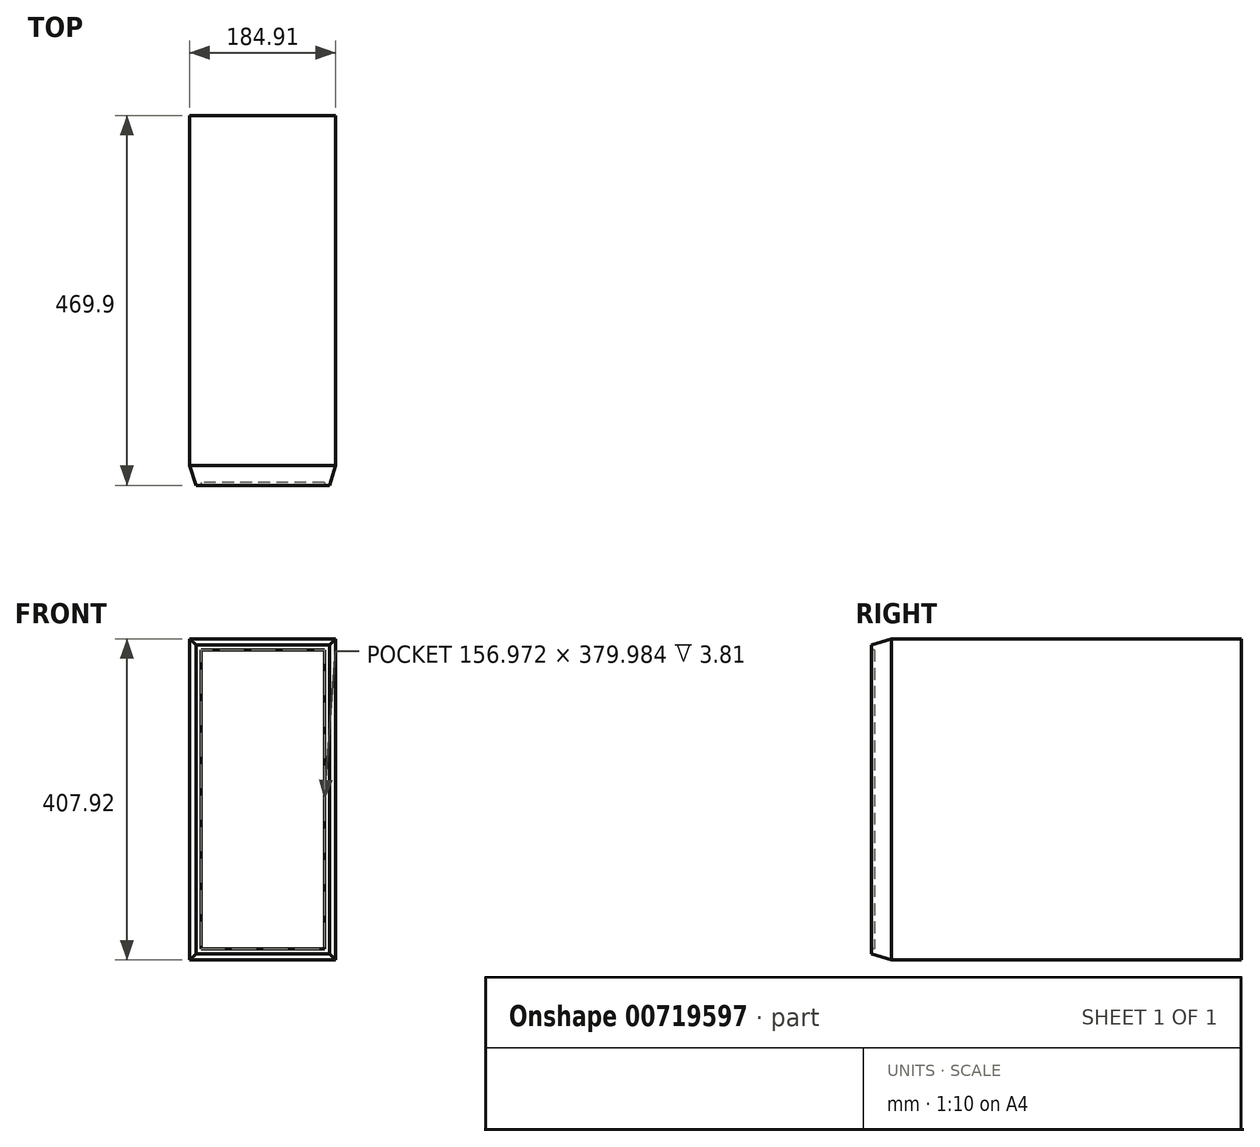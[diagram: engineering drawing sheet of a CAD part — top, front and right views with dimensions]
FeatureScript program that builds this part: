
annotation { "Feature Type Name" : "Feature", "Feature Type Description" : "" }
export const myFeature = defineFeature(function(context is Context, id is Id, definition is map)
    precondition{}
    {
        {
            var Q0;
            Q0=qCreatedBy(makeId("Front.planeOp"),FACE);
            var sketch = newSketch(context, id + "F0", { "sketchPlane" : qUnion([Q0])});
            skPoint(sketch, "E0.0", {"position": v(0, 0) * mm});
            skLineSegment(sketch, "E1.bottom", {"start": v(0, 0) * mm, "end": v(184.91, 0) * mm});
            skLineSegment(sketch, "E1.top", {"start": v(0, 407.92) * mm, "end": v(184.91, 407.92) * mm});
            skLineSegment(sketch, "E1.left", {"start": v(0, 0) * mm, "end": v(0, 407.92) * mm});
            skLineSegment(sketch, "E1.right", {"start": v(184.91, 0) * mm, "end": v(184.91, 407.92) * mm});
            skSolve(sketch);
        }
        {
            var Q0;
            Q0=makeQuery(id+"F0.imprint","IMPRINT",FACE,{"disambiguationData":[TD([[makeQuery(id+"F0.imprint","IMPRINT",EDGE,{"derivedFrom":sQuery(id+"F0.wireOp",EDGE,"E1.bottom")}),1.0]])]});
            extrude(context, id + "F1", {"entities" : qUnion([Q0]), "oppositeDirection" : true, "depth" : 469.9 * mm, "offsetDistance" : 25.4 * mm});
        }
        {
            var Q0;
            Q0=makeQuery(id+"F1.opExtrude","CAP_EDGE",EDGE,{"disambiguationData":[OSD([sQuery(id+"F0.wireOp",EDGE,"E1.left")])],"isStart":true});
            var Q1;
            Q1=makeQuery(id+"F1.opExtrude","CAP_EDGE",EDGE,{"disambiguationData":[OSD([sQuery(id+"F0.wireOp",EDGE,"E1.top")])],"isStart":true});
            var Q2;
            Q2=makeQuery(id+"F1.opExtrude","CAP_EDGE",EDGE,{"disambiguationData":[OSD([sQuery(id+"F0.wireOp",EDGE,"E1.right")])],"isStart":true});
            var Q3;
            Q3=makeQuery(id+"F1.opExtrude","CAP_EDGE",EDGE,{"disambiguationData":[OSD([sQuery(id+"F0.wireOp",EDGE,"E1.bottom")])],"isStart":true});
            chamfer(context, id + "F2", {"entities" : qUnion([Q0, Q1, Q2, Q3]), "chamferType" : ChamferType.TWO_OFFSETS, "width1" : 7.62 * mm, "oppositeDirection" : true, "width2" : 25.4 * mm, "tangentPropagation" : true});
        }
        {
            var Q0;
            Q0=makeQuery(id+"F1.opExtrude","CAP_FACE",FACE,{"disambiguationData":[OSD([sQuery(id+"F0.wireOp",EDGE,"E1.bottom"),sQuery(id+"F0.wireOp",EDGE,"E1.top"),sQuery(id+"F0.wireOp",EDGE,"E1.left"),sQuery(id+"F0.wireOp",EDGE,"E1.right")])],"isStart":true});
            var sketch = newSketch(context, id + "F3", { "sketchPlane" : qUnion([Q0])});
            skLineSegment(sketch, "E2", {"start": v(92.46, 400.3) * mm, "end": v(92.46, 7.62) * mm, "construction": true});
            skLineSegment(sketch, "E3", {"start": v(7.62, 203.96) * mm, "end": v(177.3, 203.96) * mm, "construction": true});
            skLineSegment(sketch, "E4.bottom", {"start": v(170.94, 393.95) * mm, "end": v(13.97, 393.95) * mm});
            skLineSegment(sketch, "E4.top", {"start": v(170.94, 13.97) * mm, "end": v(13.97, 13.97) * mm});
            skLineSegment(sketch, "E4.left", {"start": v(170.94, 393.95) * mm, "end": v(170.94, 13.97) * mm});
            skLineSegment(sketch, "E4.right", {"start": v(13.97, 393.95) * mm, "end": v(13.97, 13.97) * mm});
            skPoint(sketch, "E4.middle", {"position": v(92.46, 203.96) * mm});
            skSolve(sketch);
        }
        {
            var Q0;
            Q0=makeQuery(id+"F3.imprint","IMPRINT",FACE,{"disambiguationData":[TD([[makeQuery(id+"F3.imprint","IMPRINT",EDGE,{"derivedFrom":sQuery(id+"F3.wireOp",EDGE,"E4.bottom")}),1.0]])]});
            extrude(context, id + "F4", {"entities" : qUnion([Q0]), "operationType" : NewBodyOperationType.REMOVE, "oppositeDirection" : true, "depth" : 3.8 * mm, "offsetDistance" : 25.4 * mm});
        }
    });
